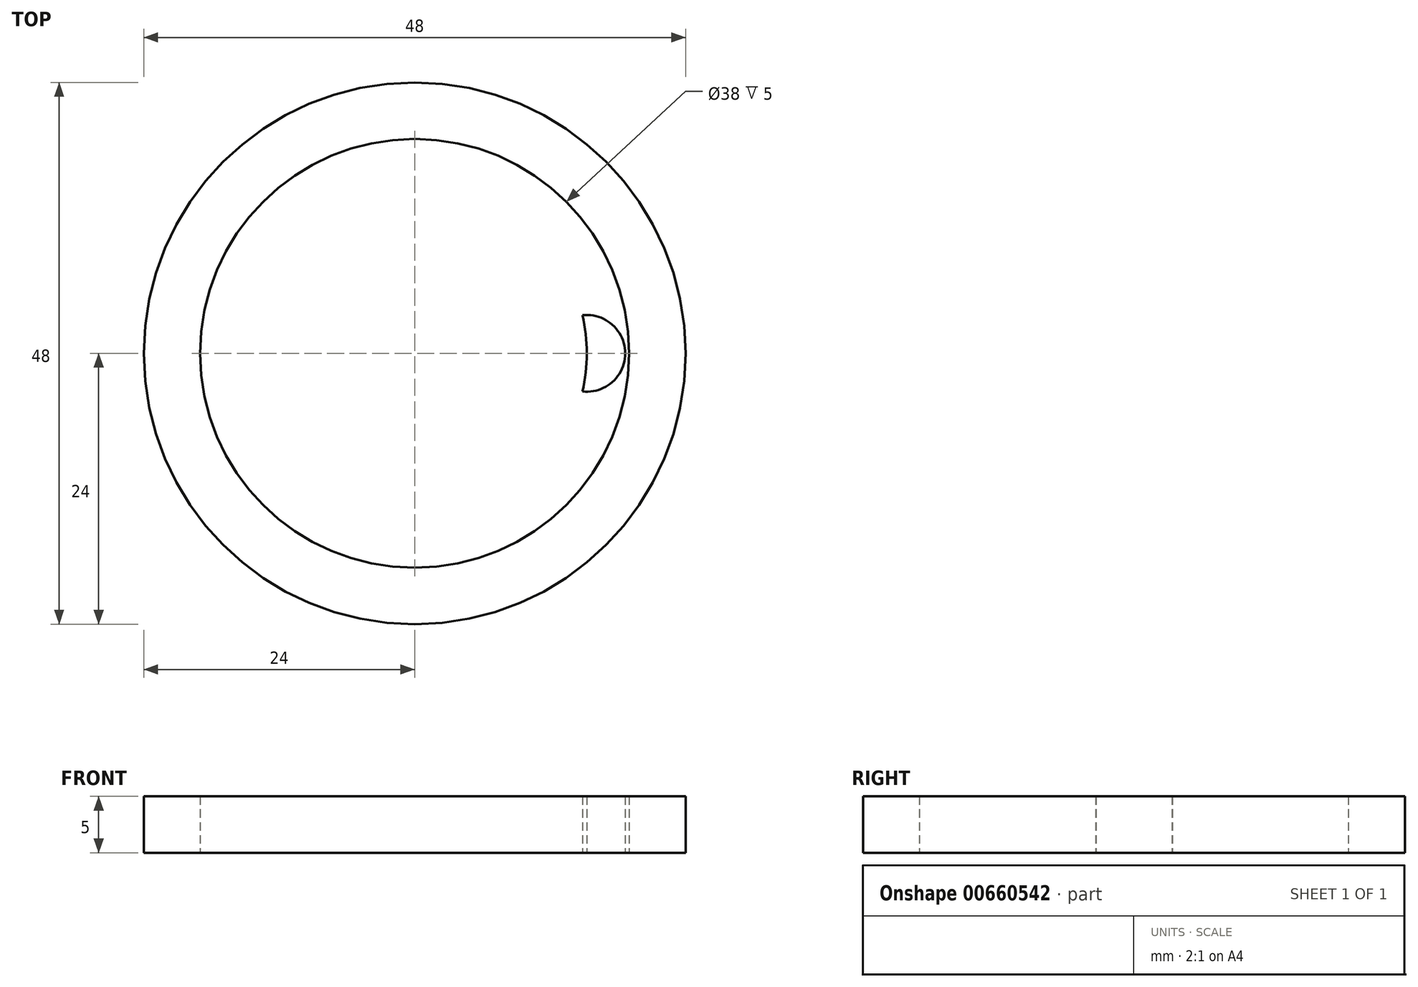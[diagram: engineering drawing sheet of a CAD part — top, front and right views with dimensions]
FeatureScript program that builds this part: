
annotation { "Feature Type Name" : "Feature", "Feature Type Description" : "" }
export const myFeature = defineFeature(function(context is Context, id is Id, definition is map)
    precondition{}
    {
        {
            var Q0;
            Q0=qCreatedBy(makeId("Top.planeOp"),FACE);
            var sketch = newSketch(context, id + "F0", { "sketchPlane" : qUnion([Q0])});
            skCircle(sketch, "E0", {"center": v(0, 0) * mm, "radius": 15.25 * mm});
            skPoint(sketch, "E1", {"position": v(-15.25, 0) * mm});
            skPoint(sketch, "E2", {"position": v(15.25, 0) * mm});
            skArc(sketch, "E3", {"start": v(14.87, 3.38) * mm, "mid": v(18.65, 0) * mm, "end": v(14.87, -3.38) * mm});
            skArc(sketch, "E4", {"start": v(-14.87, 3.38) * mm, "mid": v(-18.65, 0) * mm, "end": v(-14.87, -3.38) * mm});
            skCircle(sketch, "E5", {"center": v(0, 0) * mm, "radius": 19 * mm});
            skCircle(sketch, "E6", {"center": v(0, 0) * mm, "radius": 24 * mm});
            skLineSegment(sketch, "E7", {"start": v(0, -24) * mm, "end": v(0, -19) * mm});
            skLineSegment(sketch, "E8", {"start": v(0, 19) * mm, "end": v(0, 24) * mm});
            skPoint(sketch, "E9", {"position": v(0, -21.5) * mm});
            skPoint(sketch, "E10", {"position": v(0, 21.5) * mm});
            skSolve(sketch);
        }
        {
            var Q0;
            {var subQ0=sQuery(id+"F0.wireOp",EDGE,"E3");Q0=makeQuery(id+"F0.imprint","IMPRINT",FACE,{"disambiguationData":[TD([[makeQuery(id+"F0.imprint","IMPRINT",EDGE,{"derivedFrom":subQ0}),1.0]])]});}
            var Q1;
            Q1=makeQuery(id+"F0.imprint","IMPRINT",FACE,{"disambiguationData":[TD([[makeQuery(id+"F0.imprint","IMPRINT",EDGE,{"derivedFrom":sQuery(id+"F0.wireOp",EDGE,"E5")}),-1.0]])]});
            extrude(context, id + "F1", {"entities" : qUnion([Q0, Q1]), "depth" : 5 * mm, "offsetDistance" : 25 * mm});
        }
        {
            var Q0;
            Q0=sQuery(id+"F0.wireOp",VERTEX,"E9");
            var Q1;
            Q1=sQuery(id+"F0.wireOp",VERTEX,"E10");
            var Q2;
            Q2=makeQuery(id+"F1.opExtrude","SWEPT_BODY",BODY,{"disambiguationData":[OSD([sQuery(id+"F0.wireOp",EDGE,"E0"),sQuery(id+"F0.wireOp",EDGE,"E3"),sQuery(id+"F0.wireOp",EDGE,"E4"),sQuery(id+"F0.wireOp",EDGE,"E6")])]});
            hole(context, id + "F2", {"style" : HoleStyle.SIMPLE, "endStyle" : HoleEndStyle.THROUGH, "oppositeDirection" : true, "holeDiameter" : 3 * mm, "majorDiameter" : 5 * mm, "isTappedThrough" : true, "tappedDepth" : 12 * mm, "tapClearance" : 3, "locations" : qUnion([Q0, Q1]), "scope" : qUnion([Q2])});
        }
    });
